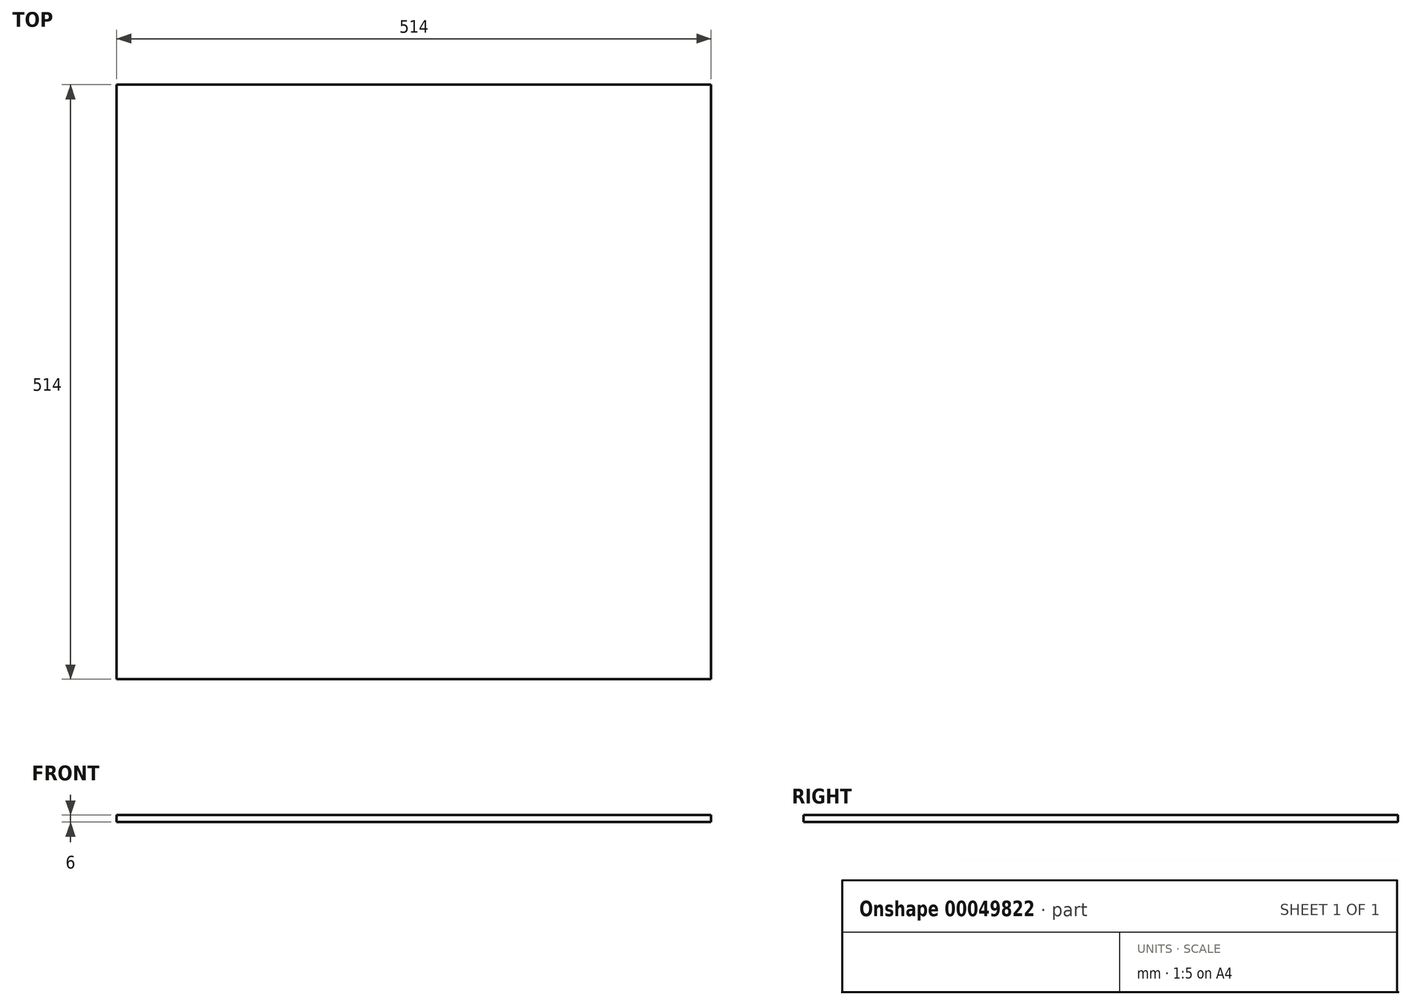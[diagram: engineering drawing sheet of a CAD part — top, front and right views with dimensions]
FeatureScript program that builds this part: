
annotation { "Feature Type Name" : "Feature", "Feature Type Description" : "" }
export const myFeature = defineFeature(function(context is Context, id is Id, definition is map)
    precondition{}
    {
        {
            var Q0;
            Q0=qCreatedBy(makeId("Top.planeOp"),FACE);
            var sketch = newSketch(context, id + "F0", { "sketchPlane" : qUnion([Q0])});
            skLineSegment(sketch, "E0.bottom", {"start": v(0, 0) * mm, "end": v(514, 0) * mm});
            skLineSegment(sketch, "E0.top", {"start": v(0, 514) * mm, "end": v(514, 514) * mm});
            skLineSegment(sketch, "E0.left", {"start": v(0, 0) * mm, "end": v(0, 514) * mm});
            skLineSegment(sketch, "E0.right", {"start": v(514, 0) * mm, "end": v(514, 514) * mm});
            skSolve(sketch);
        }
        {
            var Q0;
            Q0=qSketchRegion(id+"F0",true);
            extrude(context, id + "F1", {"entities" : qUnion([Q0]), "depth" : 6 * mm});
        }
    });
